# Revit family: IEK_РозеткаСетевая_ОткрытойУстановки_C ЗК 16А 4-местная IP20_ОКТАВА
name_source: partatom
category: Электрические приборы
units: mm (PartAtom-declared; Revit-internal decimal feet)

## family parameters
Всегда вертикально = Да
На основе рабочей плоскости = Нет
Общий = Нет
При загрузке вырезать с полостями = Нет
Размер круглого соединителя = Использовать диаметр
Сохранять ориентацию аннотаций = Да
Тип детали = Нормальный
Точка расчета площади = Нет

## types (2) — shared parameters
ADSK_URL страницы изделия = https://www.iek.ru
ADSK_Версия Revit = 2019
ADSK_Версия семейства = 1.0
ADSK_Группирование = III ЭЛЕКТРОУСТАНОВОЧНЫЕ И ЭЛЕКТРОМОНТАЖНЫЕ ИЗДЕЛИЯ
ADSK_Единица измерения = шт
ADSK_Завод-изготовитель = IEK
ADSK_Количество фаз = 1
ADSK_Количество фаз числовое = 1
ADSK_Марка = ОКТАВА
ADSK_Масса = 0.11
ADSK_Материал наименование = Пластик
ADSK_Напряжение = 220 В
IEK_URL = https://www.iek.ru
IEK_Описание = Универсальный дизайн серии открытой установки "ОКТАВА" позволяет устанавливать изделия в квартирах, загородных домах, офисных и производственных помещениях.
KSI_CMa_Строительные материалы = 01.7.14.03
KSI_CPr_Строительные изделия = 20.4.03.04 20.4.03.05 20.4.03.06
Высота = 103 мм
Глубина = 41 мм
Изготовитель = IEK
Степень защиты = IP20
Тип монтажа = Поверхность монтажа (открытая установка)
Ширина = 103 мм

## per-type parameters (varying)
| type | ADSK_Код изделия | ADSK_Материал | ADSK_Наименование | IEK_Цена за единицу |
| РС24-3-ОС | ERO41-K03-16-DC | Цвет сосна | Розетка 4-местная для открытой установки РС24-3-ОС с заземляющим контактом 16А ОКТАВА сосна IEK | 745.92 |
| РС24-3-ОК | ERO41-K33-16-DC | Цвет кремовый | Розетка 4-местная для открытой установки РС24-3-ОК с заземляющим контактом 16А ОКТАВА кремовый IEK | 475.43 |
